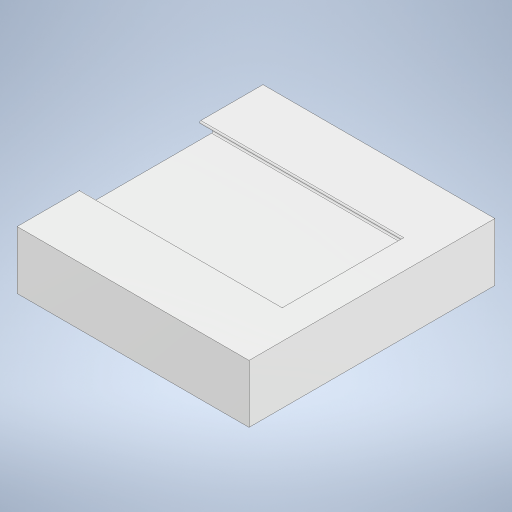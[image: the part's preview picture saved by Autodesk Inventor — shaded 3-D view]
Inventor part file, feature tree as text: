
AUTODESK INVENTOR PART (.ipt)
format: ipt  version: 2023 (Build 270158000, 158)  size: 354,816 bytes
history: native  units: mm
features: extrude x5, sketch x4, mirror x4, plane x2, fillet x2, move_body x2
ambient origin geometry x8: Origin, YZ Plane, XZ Plane, XY Plane, X Axis, Y Axis, Z Axis, Center Point
bodies: Solid1 (feature_tree)
feature tree (19):
  sketch  "Sketch1"  dims[d6=40.0mm d7=30.0mm]
  extrude  "Extrusion1"  Depth=40.0mm
  sketch  "Sketch2"  dims[d8=10.0mm d9=0.0mm d10=10.0mm]
  extrude  "Extrusion2"  Depth=10.0mm
  sketch  "Skizze7"  dims[d11=5.0mm d13=4.0mm d14=45.0deg d15=35.0mm d16=0.0mm]
  plane  "Arbeitsebene1"
  extrude  "Extrusion3"  Depth=4.0mm
  mirror  "Spiegeln1"
  fillet  "Rundung1"  [1 undecoded]
  mirror  "Spiegeln2"
  sketch  "Skizze8"  dims[d17=10.0mm d24=1.5mm d25=5.0mm d26=17.5mm d27=5.0mm d28=0.0mm d29=2.0mm d30=0.2mm d32=0.2mm d33=42.4mm d34=6.2mm d35=6.2mm d37=4.6mm d38=3.2mm d39=10.0mm d40=0.0mm d41=8.0mm d42=0.0mm d43=180.0deg d44=40.0mm d45=0.0mm d46=-40.0mm d18=0.0mm d19=0.0mm d20=0.0mm d21=0.0mm d36=0.872665mm]
  fillet  "Rundung2"  Radius=35.0mm
  extrude  "Extrusion4"  Depth=40.0mm
  mirror  "Spiegeln3"
  extrude  "Extrusion5"  Depth=40.0mm
  mirror  "Spiegeln4"
  move_body  "Move Body1"
  move_body  "Move Body2"
  plane  "Arbeitsebene2"
note: 1 required parameter value undecoded (feature->parameter linkage not recoverable at this tier; creation-order binding heuristic only, values carry confidence <= 0.55)
